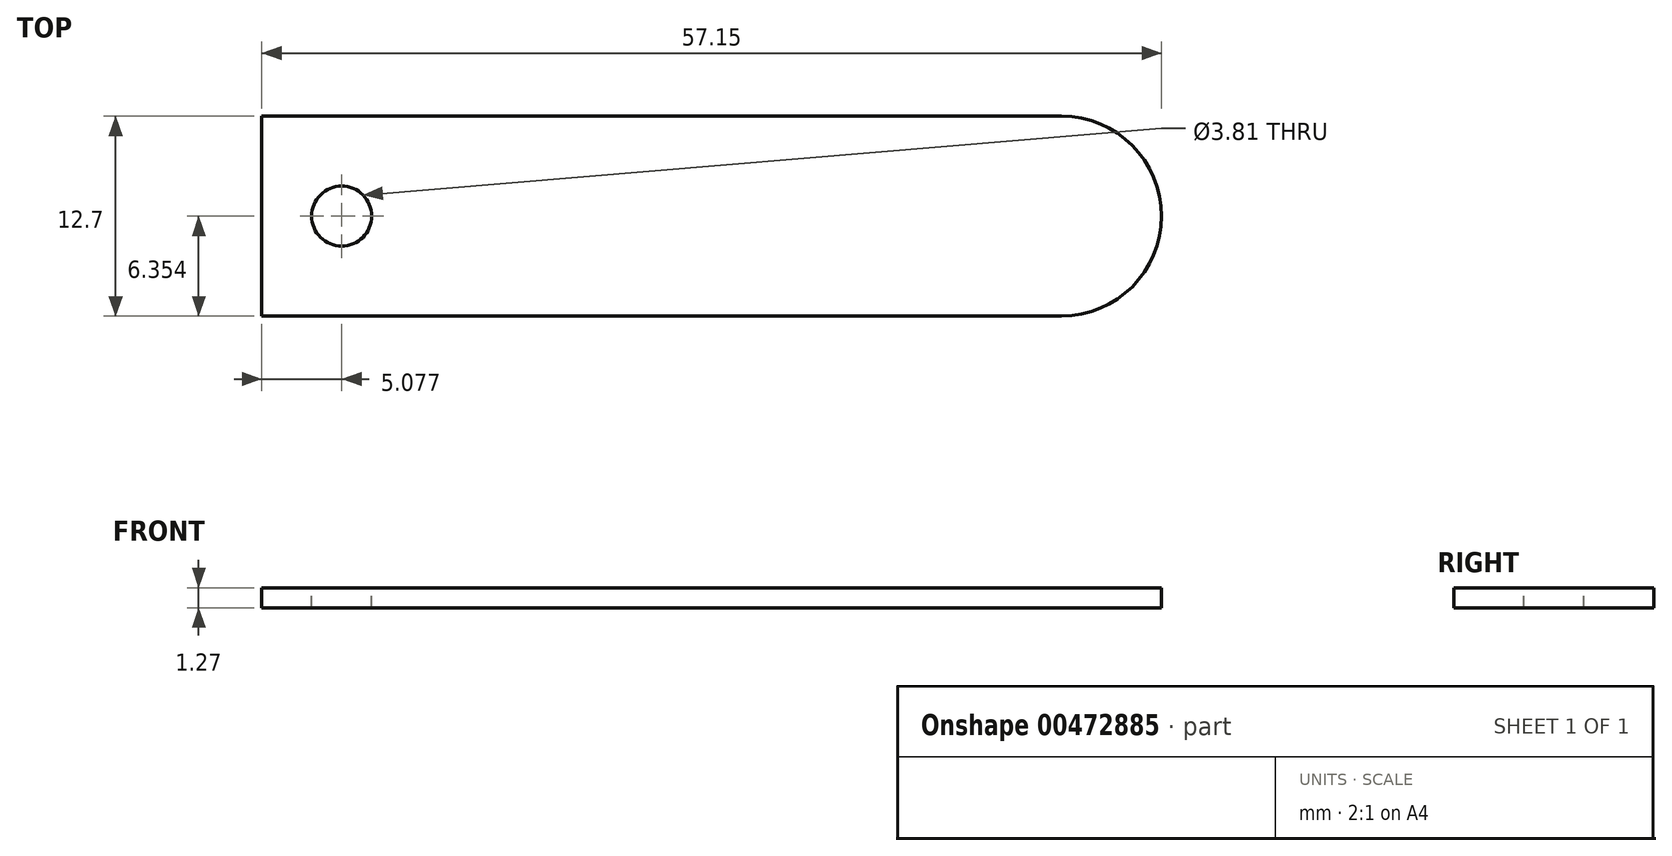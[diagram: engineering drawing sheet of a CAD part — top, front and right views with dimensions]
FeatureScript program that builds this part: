
annotation { "Feature Type Name" : "Feature", "Feature Type Description" : "" }
export const myFeature = defineFeature(function(context is Context, id is Id, definition is map)
    precondition{}
    {
        {
            var Q0;
            Q0=qCreatedBy(makeId("Top.planeOp"),FACE);
            var sketch = newSketch(context, id + "F0", { "sketchPlane" : qUnion([Q0])});
            skLineSegment(sketch, "E0.bottom", {"start": v(18.06, -27.4) * mm, "end": v(68.86, -27.4) * mm});
            skLineSegment(sketch, "E0.top", {"start": v(18.06, -14.7) * mm, "end": v(68.86, -14.7) * mm});
            skLineSegment(sketch, "E0.left", {"start": v(18.06, -27.4) * mm, "end": v(18.06, -14.7) * mm});
            skLineSegment(sketch, "E0.right", {"start": v(68.86, -27.4) * mm, "end": v(68.86, -14.7) * mm});
            skSolve(sketch);
        }
        {
            var Q0;
            Q0=makeQuery(id+"F0.imprint","IMPRINT",FACE,{"disambiguationData":[TD([[makeQuery(id+"F0.imprint","IMPRINT",EDGE,{"derivedFrom":sQuery(id+"F0.wireOp",EDGE,"E0.bottom")}),1.0]])]});
            extrude(context, id + "F1", {"entities" : qUnion([Q0]), "depth" : 1.27 * mm});
        }
        {
            var Q0;
            Q0=makeQuery(id+"F1.opExtrude","CAP_FACE",FACE,{"disambiguationData":[OSD([sQuery(id+"F0.wireOp",EDGE,"E0.bottom"),sQuery(id+"F0.wireOp",EDGE,"E0.top"),sQuery(id+"F0.wireOp",EDGE,"E0.left"),sQuery(id+"F0.wireOp",EDGE,"E0.right")])],"isStart":false});
            var sketch = newSketch(context, id + "F2", { "sketchPlane" : qUnion([Q0])});
            skCircle(sketch, "E1", {"center": v(23.14, -21.06) * mm, "radius": 1.9 * mm});
            skSolve(sketch);
        }
        {
            var Q0;
            Q0=makeQuery(id+"F2.imprint","IMPRINT",FACE,{"disambiguationData":[TD([[makeQuery(id+"F2.imprint","IMPRINT",EDGE,{"derivedFrom":sQuery(id+"F2.wireOp",EDGE,"E1")}),1.0]])]});
            extrude(context, id + "F3", {"entities" : qUnion([Q0]), "operationType" : NewBodyOperationType.REMOVE, "oppositeDirection" : true, "depth" : 25.4 * mm});
        }
        {
            var Q0;
            Q0=makeQuery(id+"F1.opExtrude","CAP_FACE",FACE,{"disambiguationData":[OSD([sQuery(id+"F0.wireOp",EDGE,"E0.bottom"),sQuery(id+"F0.wireOp",EDGE,"E0.top"),sQuery(id+"F0.wireOp",EDGE,"E0.left"),sQuery(id+"F0.wireOp",EDGE,"E0.right")])],"isStart":false});
            var sketch = newSketch(context, id + "F4", { "sketchPlane" : qUnion([Q0])});
            skCircle(sketch, "E2", {"center": v(68.86, -21.06) * mm, "radius": 6.35 * mm});
            skSolve(sketch);
        }
        {
            var Q0;
            {var subQ1=makeQuery(id+"F1.opExtrude","CAP_EDGE",EDGE,{"disambiguationData":[OSD([sQuery(id+"F0.wireOp",EDGE,"E0.right")])],"isStart":false});Q0=makeQuery(id+"F4.imprint","IMPRINT",FACE,{"disambiguationData":[TD([[makeQuery(id+"F4.imprint","IMPRINT",EDGE,{"derivedFrom":subQ1}),-1.0]])]});}
            extrude(context, id + "F5", {"entities" : qUnion([Q0]), "operationType" : NewBodyOperationType.ADD, "oppositeDirection" : true, "depth" : 1.27 * mm});
        }
    });
